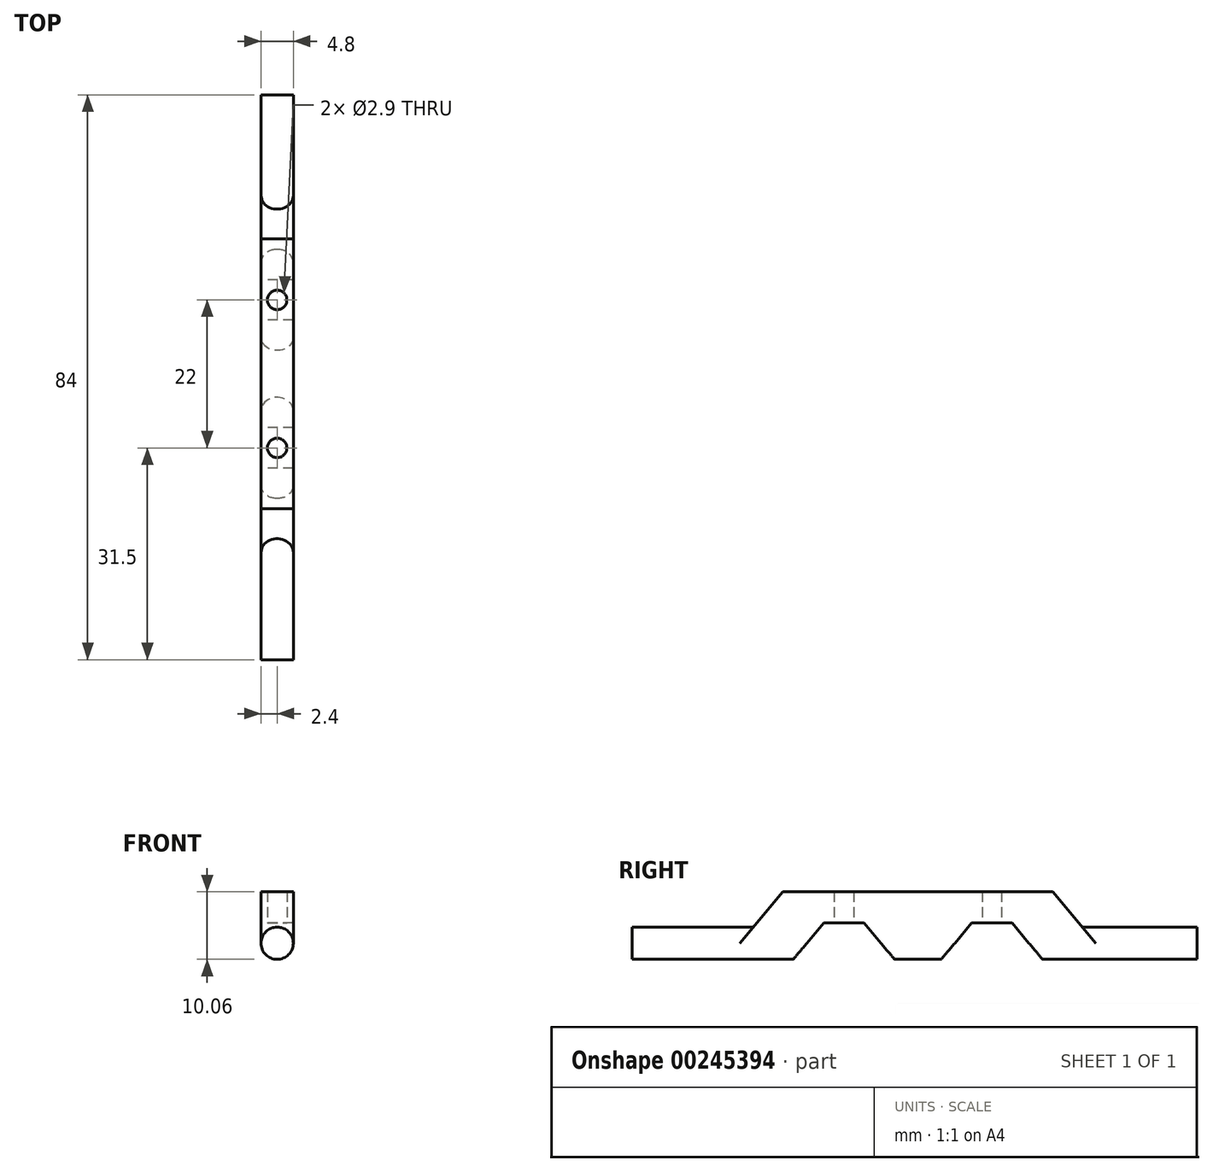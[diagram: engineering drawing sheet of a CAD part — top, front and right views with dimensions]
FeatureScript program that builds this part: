
annotation { "Feature Type Name" : "Feature", "Feature Type Description" : "" }
export const myFeature = defineFeature(function(context is Context, id is Id, definition is map)
    precondition{}
    {
        {
            var Q0;
            Q0=qCreatedBy(makeId("Front.planeOp"),FACE);
            var sketch = newSketch(context, id + "F0", { "sketchPlane" : qUnion([Q0])});
            skCircle(sketch, "E0", {"center": v(0, 0) * mm, "radius": 2.5 * mm});
            skSolve(sketch);
        }
        {
            var Q0;
            Q0=qSketchRegion(id+"F0",true);
            extrude(context, id + "F1", {"entities" : qUnion([Q0]), "depth" : 85 * mm});
        }
        {
            var Q0;
            Q0=qCreatedBy(makeId("Right.planeOp"),FACE);
            var sketch = newSketch(context, id + "F2", { "sketchPlane" : qUnion([Q0])});
            skLineSegment(sketch, "E1", {"start": v(0, 0) * mm, "end": v(-16, 0) * mm});
            skLineSegment(sketch, "E2", {"start": v(-16, 0) * mm, "end": v(-85, 0) * mm});
            skLineSegment(sketch, "E3", {"start": v(-85, 0) * mm, "end": v(-69, 0) * mm});
            skLineSegment(sketch, "E4", {"start": v(-69, 0) * mm, "end": v(-62.57, 7.66) * mm});
            skLineSegment(sketch, "E5", {"start": v(-16, 0) * mm, "end": v(-22.43, 7.66) * mm});
            skLineSegment(sketch, "E6", {"start": v(-22.43, 7.66) * mm, "end": v(-62.57, 7.66) * mm});
            skSolve(sketch);
        }
        {
            var Q0;
            Q0=qSketchRegion(id+"F2",true);
            extrude(context, id + "F3", {"entities" : qUnion([Q0]), "operationType" : NewBodyOperationType.ADD, "endBound" : BoundingType.SYMMETRIC, "depth" : 5 * mm});
        }
        {
            var Q0;
            Q0=makeQuery(id+"F3.opExtrude","CAP_FACE",FACE,{"disambiguationData":[OSD([sQuery(id+"F2.wireOp",EDGE,"E2"),sQuery(id+"F2.wireOp",EDGE,"E4"),sQuery(id+"F2.wireOp",EDGE,"E5"),sQuery(id+"F2.wireOp",EDGE,"E6")])],"isStart":true});
            var sketch = newSketch(context, id + "F4", { "sketchPlane" : qUnion([Q0])});
            skLineSegment(sketch, "E7", {"start": v(42.5, 0) * mm, "end": v(42.5, 3) * mm});
            skLineSegment(sketch, "E8", {"start": v(53.5, 3) * mm, "end": v(56.5, 3) * mm});
            skLineSegment(sketch, "E9", {"start": v(56.5, 3) * mm, "end": v(62.83, -4.54) * mm});
            skLineSegment(sketch, "E10", {"start": v(53.5, 3) * mm, "end": v(53.5, 1.19) * mm});
            skLineSegment(sketch, "E11.MirrorCS", {"start": v(53.5, 3) * mm, "end": v(50.5, 3) * mm});
            skLineSegment(sketch, "E12.MirrorCS", {"start": v(50.5, 3) * mm, "end": v(44.17, -4.54) * mm});
            skLineSegment(sketch, "E13.MirrorCS", {"start": v(34.5, 3) * mm, "end": v(40.83, -4.54) * mm});
            skLineSegment(sketch, "E14.MirrorCS", {"start": v(31.5, 3) * mm, "end": v(34.5, 3) * mm});
            skLineSegment(sketch, "E15.MirrorCS", {"start": v(31.5, 3) * mm, "end": v(28.5, 3) * mm});
            skLineSegment(sketch, "E16.MirrorCS", {"start": v(28.5, 3) * mm, "end": v(22.17, -4.54) * mm});
            skLineSegment(sketch, "E17", {"start": v(62.83, -4.54) * mm, "end": v(44.17, -4.54) * mm});
            skLineSegment(sketch, "E18", {"start": v(40.83, -4.54) * mm, "end": v(22.17, -4.54) * mm});
            skSolve(sketch);
        }
        {
            var Q0;
            Q0=qSketchRegion(id+"F4",true);
            extrude(context, id + "F5", {"entities" : qUnion([Q0]), "operationType" : NewBodyOperationType.REMOVE, "oppositeDirection" : true, "depth" : 25 * mm});
        }
        {
            var Q0;
            Q0=makeQuery(id+"F5.boolean.opBoolean","COPY",FACE,{"derivedFrom":makeQuery(id+"F5.opExtrude","SWEPT_FACE",FACE,{"disambiguationData":[OSD([sQuery(id+"F4.wireOp",EDGE,"E8"),sQuery(id+"F4.wireOp",EDGE,"E11.MirrorCS")])]})});
            var sketch = newSketch(context, id + "F6", { "sketchPlane" : qUnion([Q0])});
            skLineSegment(sketch, "E19", {"start": v(0, 56.5) * mm, "end": v(0, 50.5) * mm});
            skCircle(sketch, "E20", {"center": v(0, 53.5) * mm, "radius": 1.45 * mm});
            skSolve(sketch);
        }
        {
            var Q0;
            Q0=makeQuery(id+"F3.opExtrude","CAP_FACE",FACE,{"disambiguationData":[OSD([sQuery(id+"F2.wireOp",EDGE,"E2"),sQuery(id+"F2.wireOp",EDGE,"E4"),sQuery(id+"F2.wireOp",EDGE,"E5"),sQuery(id+"F2.wireOp",EDGE,"E6")])],"isStart":true});
            var sketch = newSketch(context, id + "F7", { "sketchPlane" : qUnion([Q0])});
            skLineSegment(sketch, "E21", {"start": v(53.5, 3) * mm, "end": v(53.5, 7.5) * mm});
            skLineSegment(sketch, "E22", {"start": v(53.5, 7.5) * mm, "end": v(19.92, 7.5) * mm});
            skLineSegment(sketch, "E23", {"start": v(19.92, 7.5) * mm, "end": v(19.92, 10.39) * mm});
            skLineSegment(sketch, "E24", {"start": v(19.92, 10.39) * mm, "end": v(66.52, 10.39) * mm});
            skLineSegment(sketch, "E25", {"start": v(66.52, 10.39) * mm, "end": v(66.52, 7.5) * mm});
            skLineSegment(sketch, "E26", {"start": v(66.52, 7.5) * mm, "end": v(53.5, 7.5) * mm});
            skSolve(sketch);
        }
        {
            var Q0;
            {var subQ2=sQuery(id+"F7.wireOp",EDGE,"E23");Q0=makeQuery(id+"F7.imprint","IMPRINT",FACE,{"disambiguationData":[TD([[makeQuery(id+"F7.imprint","IMPRINT",EDGE,{"derivedFrom":subQ2}),-1.0]])]});}
            extrude(context, id + "F8", {"entities" : qUnion([Q0]), "operationType" : NewBodyOperationType.REMOVE, "oppositeDirection" : true, "depth" : 25 * mm});
        }
        {
            var Q0;
            Q0=qSketchRegion(id+"F6",true);
            extrude(context, id + "F9", {"entities" : qUnion([Q0]), "operationType" : NewBodyOperationType.REMOVE, "oppositeDirection" : true, "depth" : 25 * mm});
        }
        {
            var Q0;
            Q0=makeQuery(id+"F5.boolean.opBoolean","COPY",FACE,{"derivedFrom":makeQuery(id+"F5.opExtrude","SWEPT_FACE",FACE,{"disambiguationData":[OSD([sQuery(id+"F4.wireOp",EDGE,"E14.MirrorCS"),sQuery(id+"F4.wireOp",EDGE,"E15.MirrorCS")])]})});
            var sketch = newSketch(context, id + "F10", { "sketchPlane" : qUnion([Q0])});
            skLineSegment(sketch, "E27", {"start": v(0, 34.5) * mm, "end": v(0, 28.5) * mm});
            skCircle(sketch, "E28", {"center": v(0, 31.5) * mm, "radius": 1.45 * mm});
            skSolve(sketch);
        }
        {
            var Q0;
            Q0=qSketchRegion(id+"F10",true);
            extrude(context, id + "F11", {"entities" : qUnion([Q0]), "operationType" : NewBodyOperationType.REMOVE, "oppositeDirection" : true, "depth" : 25 * mm});
        }
        {
            var Q0;
            Q0=makeQuery(id+"F1.opExtrude","CAP_FACE",FACE,{"disambiguationData":[OSD([sQuery(id+"F0.wireOp",EDGE,"E0")])],"isStart":false});
            var sketch = newSketch(context, id + "F12", { "sketchPlane" : qUnion([Q0])});
            skLineSegment(sketch, "E29", {"start": v(0, 0) * mm, "end": v(0, -3.5) * mm});
            skCircle(sketch, "E30", {"center": v(0, 0) * mm, "radius": 23.75 * mm});
            skCircle(sketch, "E31", {"center": v(0, 0) * mm, "radius": 13.75 * mm});
            skLineSegment(sketch, "E32", {"start": v(0, -3.5) * mm, "end": v(23.5, -3.5) * mm});
            skCircle(sketch, "E33", {"center": v(0, 0) * mm, "radius": 16.75 * mm});
            skCircle(sketch, "E34", {"center": v(0, 0) * mm, "radius": 20.75 * mm});
            skLineSegment(sketch, "E35", {"start": v(0, 0) * mm, "end": v(2.5, 0) * mm});
            skLineSegment(sketch, "E36", {"start": v(2.5, 0) * mm, "end": v(2.5, 28) * mm});
            skLineSegment(sketch, "E37", {"start": v(0, 0) * mm, "end": v(0, -1.5) * mm});
            skLineSegment(sketch, "E38", {"start": v(0, -1.5) * mm, "end": v(23.7, -1.5) * mm});
            skSolve(sketch);
        }
        {
            var Q0;
            {var subQ4=sQuery(id+"F12.wireOp",EDGE,"E35");Q0=makeQuery(id+"F12.imprint","IMPRINT",FACE,{"disambiguationData":[TD([[makeQuery(id+"F12.imprint","IMPRINT",EDGE,{"derivedFrom":subQ4}),1.0]])]});}
            var sketch = newSketch(context, id + "F13", { "sketchPlane" : qUnion([Q0])});
            skArc(sketch, "E39", {"start": v(-2.4, 0) * mm, "mid": v(0, -2.4) * mm, "end": v(2.4, 0) * mm});
            skLineSegment(sketch, "E40", {"start": v(-2.4, 0) * mm, "end": v(-2.4, 9.77) * mm});
            skLineSegment(sketch, "E41", {"start": v(-2.4, 9.77) * mm, "end": v(-6.2, 9.77) * mm});
            skLineSegment(sketch, "E42", {"start": v(-6.2, 9.77) * mm, "end": v(-6.2, -5.76) * mm});
            skLineSegment(sketch, "E43", {"start": v(-6.2, -5.76) * mm, "end": v(5.57, -5.76) * mm});
            skLineSegment(sketch, "E44", {"start": v(5.57, -5.76) * mm, "end": v(5.57, 8.85) * mm});
            skLineSegment(sketch, "E45", {"start": v(2.4, 0) * mm, "end": v(2.4, 9.16) * mm});
            skLineSegment(sketch, "E46", {"start": v(2.4, 9.16) * mm, "end": v(5.57, 8.85) * mm});
            skSolve(sketch);
        }
        {
            var Q0;
            Q0=qSketchRegion(id+"F13",true);
            extrude(context, id + "F14", {"entities" : qUnion([Q0]), "operationType" : NewBodyOperationType.REMOVE, "oppositeDirection" : true, "depth" : 102 * mm});
        }
        {
            var Q0;
            {var subQ4=sQuery(id+"F12.wireOp",EDGE,"E35");Q0=makeQuery(id+"F12.imprint","IMPRINT",FACE,{"disambiguationData":[TD([[makeQuery(id+"F12.imprint","IMPRINT",EDGE,{"derivedFrom":subQ4}),1.0]])]});}
            var sketch = newSketch(context, id + "F15", { "sketchPlane" : qUnion([Q0])});
            skArc(sketch, "E47", {"start": v(2.4, 0) * mm, "mid": v(0, 2.4) * mm, "end": v(-2.4, 0) * mm});
            skLineSegment(sketch, "E48", {"start": v(2.4, 0) * mm, "end": v(4.83, 0) * mm});
            skLineSegment(sketch, "E49", {"start": v(4.83, 0) * mm, "end": v(4.18, 8.08) * mm});
            skLineSegment(sketch, "E50", {"start": v(4.18, 8.08) * mm, "end": v(-2.94, 8.08) * mm});
            skLineSegment(sketch, "E51", {"start": v(-2.94, 8.08) * mm, "end": v(-3.46, 0) * mm});
            skLineSegment(sketch, "E52", {"start": v(-3.46, 0) * mm, "end": v(-2.4, 0) * mm});
            skSolve(sketch);
        }
        {
            var Q0;
            Q0=qSketchRegion(id+"F15",true);
            var Q1;
            Q1=makeQuery(id+"F3.opExtrude","SWEPT_FACE",FACE,{"disambiguationData":[OSD([sQuery(id+"F2.wireOp",EDGE,"E4")])]});
            extrude(context, id + "F16", {"entities" : qUnion([Q0]), "operationType" : NewBodyOperationType.REMOVE, "endBound" : BoundingType.UP_TO_SURFACE, "oppositeDirection" : true, "endBoundEntityFace" : qUnion([Q1]), "depth" : 25 * mm});
        }
        {
            var Q0;
            Q0=makeQuery(id+"F1.opExtrude","CAP_FACE",FACE,{"disambiguationData":[OSD([sQuery(id+"F0.wireOp",EDGE,"E0")])],"isStart":true});
            var sketch = newSketch(context, id + "F17", { "sketchPlane" : qUnion([Q0])});
            skArc(sketch, "E53", {"start": v(2.4, 0) * mm, "mid": v(0, 2.4) * mm, "end": v(-2.4, 0) * mm});
            skLineSegment(sketch, "E54", {"start": v(3.9, 0) * mm, "end": v(4.32, 8.69) * mm});
            skLineSegment(sketch, "E55", {"start": v(4.32, 8.69) * mm, "end": v(-4.98, 8.37) * mm});
            skLineSegment(sketch, "E56", {"start": v(-4.98, 8.37) * mm, "end": v(-3.42, 0) * mm});
            skLineSegment(sketch, "E57", {"start": v(-3.42, 0) * mm, "end": v(-2.4, 0) * mm});
            skLineSegment(sketch, "E58", {"start": v(2.4, 0) * mm, "end": v(3.9, 0) * mm});
            skSolve(sketch);
        }
        {
            var Q0;
            Q0=qSketchRegion(id+"F17",true);
            var Q1;
            Q1=makeQuery(id+"F3.opExtrude","SWEPT_FACE",FACE,{"disambiguationData":[OSD([sQuery(id+"F2.wireOp",EDGE,"E5")])]});
            extrude(context, id + "F18", {"entities" : qUnion([Q0]), "operationType" : NewBodyOperationType.REMOVE, "endBound" : BoundingType.UP_TO_SURFACE, "oppositeDirection" : true, "endBoundEntityFace" : qUnion([Q1]), "depth" : 25 * mm});
        }
        {
            var Q0;
            Q0=makeQuery(id+"F1.opExtrude","CAP_FACE",FACE,{"disambiguationData":[OSD([sQuery(id+"F0.wireOp",EDGE,"E0")])],"isStart":true});
            extrude(context, id + "F19", {"entities" : qUnion([Q0]), "operationType" : NewBodyOperationType.REMOVE, "oppositeDirection" : true, "depth" : 1 * mm, "offsetDistance" : 25 * mm});
        }
    });
